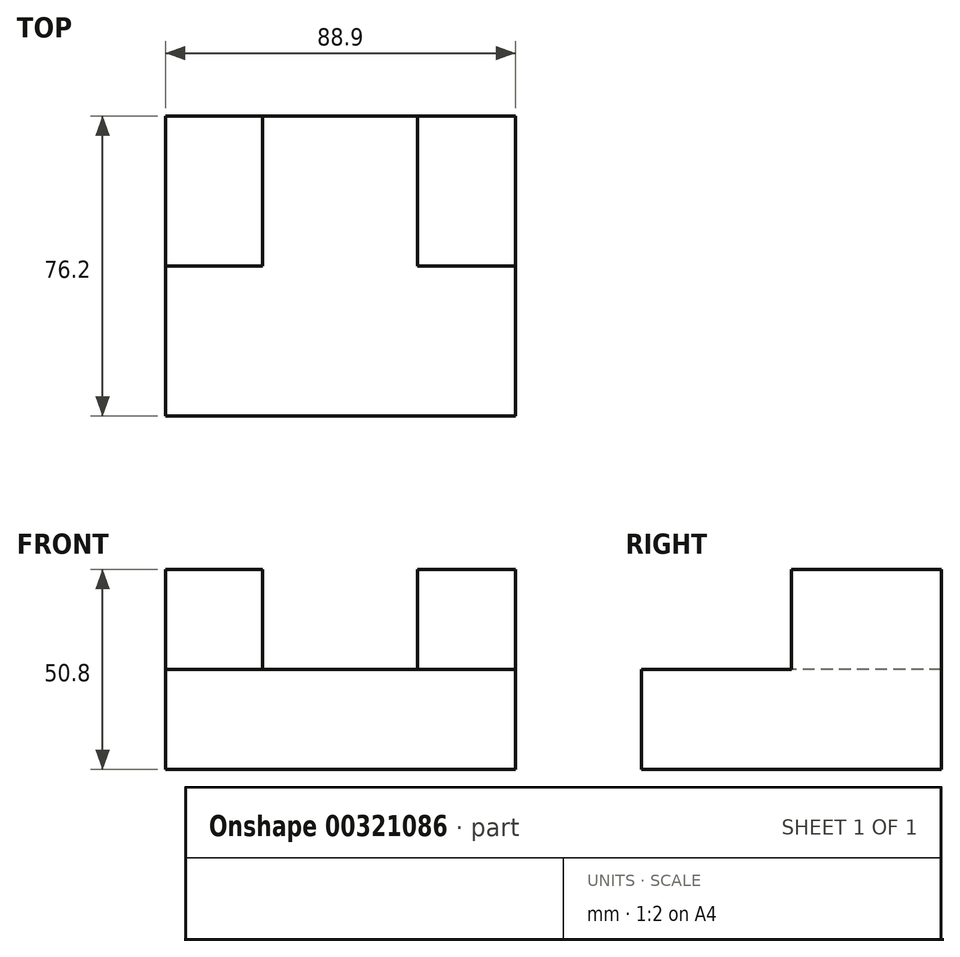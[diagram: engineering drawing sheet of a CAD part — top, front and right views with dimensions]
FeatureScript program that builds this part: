
annotation { "Feature Type Name" : "Feature", "Feature Type Description" : "" }
export const myFeature = defineFeature(function(context is Context, id is Id, definition is map)
    precondition{}
    {
        {
            var Q0;
            Q0=qCreatedBy(makeId("Right.planeOp"),FACE);
            var sketch = newSketch(context, id + "F0", { "sketchPlane" : qUnion([Q0])});
            skLineSegment(sketch, "E0", {"start": v(-35.53, -27.63) * mm, "end": v(40.67, -27.63) * mm});
            skLineSegment(sketch, "E1", {"start": v(40.67, -27.63) * mm, "end": v(40.67, 23.17) * mm});
            skLineSegment(sketch, "E2", {"start": v(40.67, 23.17) * mm, "end": v(2.57, 23.17) * mm});
            skLineSegment(sketch, "E3", {"start": v(2.57, 23.17) * mm, "end": v(2.57, -2.23) * mm});
            skLineSegment(sketch, "E4", {"start": v(2.57, -2.23) * mm, "end": v(-35.53, -2.23) * mm});
            skLineSegment(sketch, "E5", {"start": v(-35.53, -2.23) * mm, "end": v(-35.53, -27.63) * mm});
            skSolve(sketch);
        }
        {
            var Q0;
            Q0 = qSketchRegion(id + "F0", true);
            var Q1;
            Q1=makeQuery(id+"F0.imprint","IMPRINT",FACE,{"disambiguationData":[TD([[makeQuery(id+"F0.imprint","IMPRINT",EDGE,{"derivedFrom":sQuery(id+"F0.wireOp",EDGE,"E0")}),1.0]])]});
            extrude(context, id + "F1", {"entities" : qUnion([Q0, Q1]), "depth" : 88.9 * mm});
        }
        {
            var Q0;
            Q0=makeQuery(id+"F1.opExtrude","SWEPT_FACE",FACE,{"disambiguationData":[OSD([sQuery(id+"F0.wireOp",EDGE,"E3")])]});
            var sketch = newSketch(context, id + "F2", { "sketchPlane" : qUnion([Q0])});
            skLineSegment(sketch, "E6", {"start": v(44.45, -2.23) * mm, "end": v(44.45, 23.17) * mm});
            skLineSegment(sketch, "E7", {"start": v(25.91, -2.23) * mm, "end": v(64.01, -2.23) * mm});
            skLineSegment(sketch, "E8", {"start": v(25.91, -2.23) * mm, "end": v(25.91, 23.17) * mm});
            skLineSegment(sketch, "E9", {"start": v(25.91, 23.17) * mm, "end": v(64.01, 23.17) * mm});
            skLineSegment(sketch, "E10", {"start": v(64.01, 23.17) * mm, "end": v(64.01, -2.23) * mm});
            skSolve(sketch);
        }
        {
            var Q0;
            {var subQ0=sQuery(id+"F2.wireOp",EDGE,"E6");Q0=makeQuery(id+"F2.imprint","IMPRINT",FACE,{"disambiguationData":[TD([[makeQuery(id+"F2.imprint","IMPRINT",EDGE,{"derivedFrom":subQ0}),-1.0]])]});}
            extrude(context, id + "F3", {"entities" : qUnion([Q0]), "operationType" : NewBodyOperationType.REMOVE, "endBound" : BoundingType.THROUGH_ALL, "oppositeDirection" : true, "depth" : 25.4 * mm});
        }
        {
            var Q0;
            Q0=makeQuery(id+"F3.boolean.opBoolean","COPY",FACE,{"derivedFrom":makeQuery(id+"F3.opExtrude","SWEPT_FACE",FACE,{"disambiguationData":[OSD([sQuery(id+"F2.wireOp",EDGE,"E6")])]})});
            extrude(context, id + "F4", {"entities" : qUnion([Q0]), "operationType" : NewBodyOperationType.REMOVE, "oppositeDirection" : true, "depth" : 19.8 * mm});
        }
    });
